# Revit family: Fireplace_Gas_Heatilator_See-Through
name_source: partatom
category: Mechanical Equipment
revit_build: Autodesk Revit 2015 (Build: 20140323_1530(x64)
units: mm (PartAtom-declared; Revit-internal decimal feet)

## types (6) — shared parameters
Assembly Code = D3020
Construction Details = http://www.arcat.com
Default Elevation = 0' - 0"
Electrical_Voltage = 120 V
Fixture Finish = Metal - Heatilator - Metallic Black
Fuel Consumption = as Specified
HVAC_BTU Output = 0.0 Btu/h
Heating Capacity = as Specified
Keynote = 10305
Manufacturer = Heatilator
Manufacturer Website = http://www.heatilator.com
Product Data = http://www.arcat.com
Revision = R2_2014-09
Sales Information = http://www.heatilator.com
Send Message = http://www.arcat.com
Specification = http://www.arcat.com
Standards Conformance = cULus
URL = http://www.heatilator.com
zero-valued in all types: Expected Lifespan (Years), Maintenance Schedule (Months), Unit Weight, Warranty Duration (Years)

## per-type parameters (varying)
| type | Description | Efficiency Ratings | Fuel Type | HVAC_BTU Input | Model | Opening Height | Opening Width | Unit Depth | Unit Height | Unit Width |
| 36x25 Viewing Area B Vent LP | Heatilator Gas Burning Fireplace - See-Through GBST4336 as Specified | Steady State 72  ;  AFUE 53  ;  EnerGuide 59 | LP | 36000.0 Btu/h | GBST4336 | 2' - 0 1/2" | 3' - 0" | 2' - 0" | 2' - 10 5/8" | 3' - 6" |
| 36x25 Viewing Area B Vent NG | Heatilator Gas Burning Fireplace - See-Through GBST4336 as Specified | Steady State 72  ;  AFUE 53  ;  EnerGuide 59 | NG | 37000.0 Btu/h | GBST4336 | 2' - 0 1/2" | 3' - 0" | 2' - 0" | 2' - 10 5/8" | 3' - 6" |
| 36x25 Viewing Area Direct Vent LP | Heatilator Gas Burning Fireplace - See-Through GDST4336 as Specified | Steady State 72  ;  AFUE 53  ;  EnerGuide 59 | LP | 36000.0 Btu/h | GDST4336 | 2' - 0 1/2" | 3' - 0" | 2' - 0" | 2' - 10 5/8" | 3' - 6" |
| 36x25 Viewing Area Direct Vent NG | Heatilator Gas Burning Fireplace - See-Through GDST4336 as Specified | Steady State 72  ;  AFUE 53  ;  EnerGuide 59 | NG | 37000.0 Btu/h | GDST4336 | 2' - 0 1/2" | 3' - 0" | 2' - 0" | 2' - 10 5/8" | 3' - 6" |
| 31x21 Viewing Area LP | Heatilator Gas Burning Fireplace - See-Through GDST3831 as Specified | Steady State 74  ;  AFUE 47  ;  EnerGuide 51 | LP | 20000.0 Btu/h | GDST3831 | 1' - 9" | 2' - 7 1/8" | 1' - 4" | 2' - 7 1/4" | 3' - 1 1/8" |
| 31x21 Viewing Area NG | Heatilator Gas Burning Fireplace - See-Through GDST3831 as Specified | Steady State 74  ;  AFUE 47  ;  EnerGuide 51 | NG | 21000.0 Btu/h | GDST3831 | 1' - 9" | 2' - 7 1/8" | 1' - 4" | 2' - 7 1/4" | 3' - 1 1/8" |

## geometry (parser evidence)
native form markers: Blend x8, Sweep x5
no freeform markers — native parametric forms only
